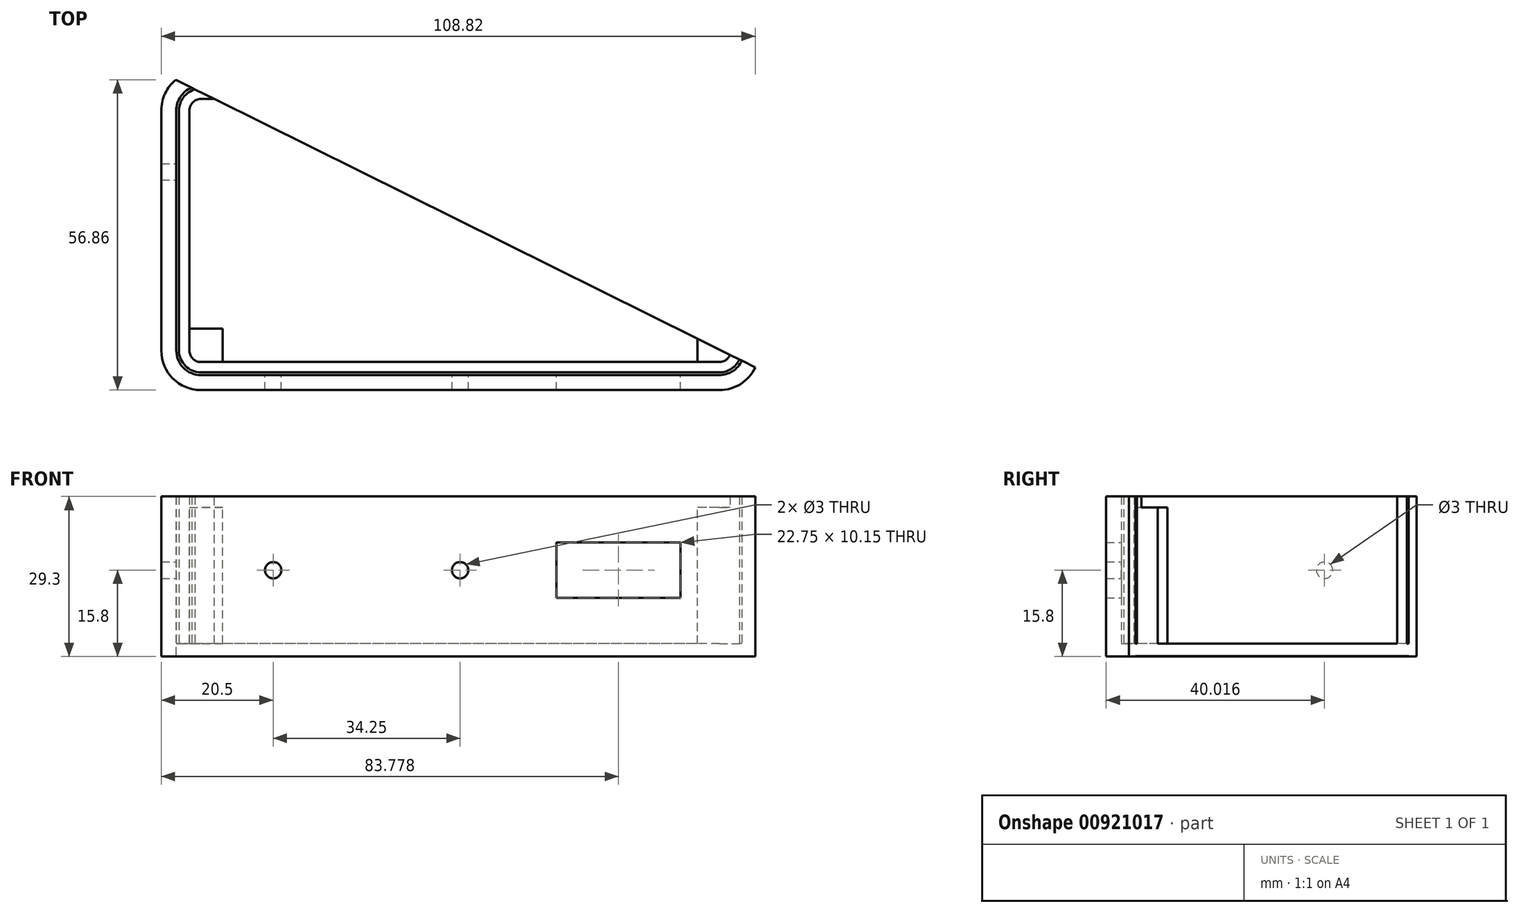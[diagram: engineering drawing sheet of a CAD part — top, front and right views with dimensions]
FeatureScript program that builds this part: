
annotation { "Feature Type Name" : "Feature", "Feature Type Description" : "" }
export const myFeature = defineFeature(function(context is Context, id is Id, definition is map)
    precondition{}
    {
        {
            var Q0;
            Q0=qCreatedBy(makeId("Top.planeOp"),FACE);
            var sketch = newSketch(context, id + "F0", { "sketchPlane" : qUnion([Q0])});
            skLineSegment(sketch, "E0.bottom", {"start": v(47.5, 26) * mm, "end": v(-47.5, 26) * mm});
            skLineSegment(sketch, "E0.top", {"start": v(47.5, -26) * mm, "end": v(-47.5, -26) * mm});
            skLineSegment(sketch, "E0.left", {"start": v(51.5, 22) * mm, "end": v(51.5, -22) * mm});
            skLineSegment(sketch, "E0.right", {"start": v(-51.5, 22) * mm, "end": v(-51.5, -22) * mm});
            skPoint(sketch, "E0.middle", {"position": v(0, 0) * mm});
            skPoint(sketch, "E1.visualSharp", {"position": v(-51.5, 26) * mm});
            skArc(sketch, "E1.filletArc", {"start": v(-47.5, 26) * mm, "mid": v(-50.33, 24.83) * mm, "end": v(-51.5, 22) * mm});
            skPoint(sketch, "E2.visualSharp", {"position": v(-51.5, -26) * mm});
            skArc(sketch, "E2.filletArc", {"start": v(-51.5, -22) * mm, "mid": v(-50.33, -24.83) * mm, "end": v(-47.5, -26) * mm});
            skPoint(sketch, "E3.visualSharp", {"position": v(51.5, -26) * mm});
            skArc(sketch, "E3.filletArc", {"start": v(47.5, -26) * mm, "mid": v(50.33, -24.83) * mm, "end": v(51.5, -22) * mm});
            skPoint(sketch, "E4.visualSharp", {"position": v(51.5, 26) * mm});
            skArc(sketch, "E4.filletArc", {"start": v(51.5, 22) * mm, "mid": v(50.33, 24.83) * mm, "end": v(47.5, 26) * mm});
            skLineSegment(sketch, "E5", {"start": v(-51.5, 18) * mm, "end": v(-43.5, 18) * mm});
            skLineSegment(sketch, "E6", {"start": v(-43.5, 18) * mm, "end": v(-43.5, 26) * mm});
            skLineSegment(sketch, "E7.MirrorCS", {"start": v(-43.5, -18) * mm, "end": v(-43.5, -26) * mm});
            skLineSegment(sketch, "E8.MirrorCS", {"start": v(-51.5, -18) * mm, "end": v(-43.5, -18) * mm});
            skLineSegment(sketch, "E9.MirrorCS", {"start": v(43.5, 18) * mm, "end": v(43.5, 26) * mm});
            skLineSegment(sketch, "E10.MirrorCS", {"start": v(51.5, 18) * mm, "end": v(43.5, 18) * mm});
            skLineSegment(sketch, "E11.MirrorCS", {"start": v(51.5, -18) * mm, "end": v(43.5, -18) * mm});
            skLineSegment(sketch, "E12.MirrorCS", {"start": v(43.5, -18) * mm, "end": v(43.5, -26) * mm});
            skSolve(sketch);
        }
        {
            var Q0;
            {var subQ3=sQuery(id+"F0.wireOp",EDGE,"E5");Q0=makeQuery(id+"F0.imprint","IMPRINT",FACE,{"disambiguationData":[TD([[makeQuery(id+"F0.imprint","IMPRINT",EDGE,{"derivedFrom":subQ3}),-1.0]])]});}
            var Q1;
            {var subQ1=sQuery(id+"F0.wireOp",EDGE,"E1.filletArc");Q1=makeQuery(id+"F0.imprint","IMPRINT",FACE,{"disambiguationData":[TD([[makeQuery(id+"F0.imprint","IMPRINT",EDGE,{"derivedFrom":subQ1}),1.0]])]});}
            var Q2;
            {var subQ0=sQuery(id+"F0.wireOp",EDGE,"E4.filletArc");Q2=makeQuery(id+"F0.imprint","IMPRINT",FACE,{"disambiguationData":[TD([[makeQuery(id+"F0.imprint","IMPRINT",EDGE,{"derivedFrom":subQ0}),1.0]])]});}
            var Q3;
            {var subQ1=sQuery(id+"F0.wireOp",EDGE,"E3.filletArc");Q3=makeQuery(id+"F0.imprint","IMPRINT",FACE,{"disambiguationData":[TD([[makeQuery(id+"F0.imprint","IMPRINT",EDGE,{"derivedFrom":subQ1}),1.0]])]});}
            var Q4;
            {var subQ1=sQuery(id+"F0.wireOp",EDGE,"E2.filletArc");Q4=makeQuery(id+"F0.imprint","IMPRINT",FACE,{"disambiguationData":[TD([[makeQuery(id+"F0.imprint","IMPRINT",EDGE,{"derivedFrom":subQ1}),1.0]])]});}
            extrude(context, id + "F1", {"entities" : qUnion([Q0, Q1, Q2, Q3, Q4]), "depth" : 27 * mm, "offsetDistance" : 25 * mm});
        }
        {
            var Q0;
            Q0=makeQuery(id+"F1.opExtrude","CAP_FACE",FACE,{"disambiguationData":[OSD([sQuery(id+"F0.wireOp",EDGE,"E0.bottom"),sQuery(id+"F0.wireOp",EDGE,"E0.top"),sQuery(id+"F0.wireOp",EDGE,"E0.left"),sQuery(id+"F0.wireOp",EDGE,"E0.right"),sQuery(id+"F0.wireOp",EDGE,"E1.filletArc"),sQuery(id+"F0.wireOp",EDGE,"E2.filletArc"),sQuery(id+"F0.wireOp",EDGE,"E3.filletArc"),sQuery(id+"F0.wireOp",EDGE,"E4.filletArc")])],"isStart":false});
            shell(context, id + "F2", {"entities" : qUnion([Q0]), "thickness" : 1.9 * mm});
        }
        {
            var Q0;
            Q0=makeQuery(id+"F0.imprint","IMPRINT",FACE,{"disambiguationData":[TD([[makeQuery(id+"F0.imprint","IMPRINT",EDGE,{"derivedFrom":sQuery(id+"F0.wireOp",EDGE,"E0.bottom")}),1.0]])]});
            var sketch = newSketch(context, id + "F3", { "sketchPlane" : qUnion([Q0])});
            skLineSegment(sketch, "E13", {"start": v(-51.48, 17.9) * mm, "end": v(-43.48, 17.9) * mm});
            skLineSegment(sketch, "E14", {"start": v(-43.48, 17.9) * mm, "end": v(-43.48, 25.9) * mm});
            skLineSegment(sketch, "E15.MirrorCS", {"start": v(-43.48, -17.9) * mm, "end": v(-43.48, -25.9) * mm});
            skLineSegment(sketch, "E16.MirrorCS", {"start": v(-51.48, -17.9) * mm, "end": v(-43.48, -17.9) * mm});
            skLineSegment(sketch, "E17.MirrorCS", {"start": v(43.48, 17.9) * mm, "end": v(43.48, 25.9) * mm});
            skLineSegment(sketch, "E18.MirrorCS", {"start": v(51.48, 17.9) * mm, "end": v(43.48, 17.9) * mm});
            skLineSegment(sketch, "E19.MirrorCS", {"start": v(51.48, -17.9) * mm, "end": v(43.48, -17.9) * mm});
            skLineSegment(sketch, "E20.MirrorCS", {"start": v(43.48, -17.9) * mm, "end": v(43.48, -25.9) * mm});
            skSolve(sketch);
        }
        {
            var Q0;
            {var subQ0=sQuery(id+"F0.wireOp",EDGE,"E1.filletArc");Q0=makeQuery(id+"F3.imprint","IMPRINT",FACE,{"disambiguationData":[TD([[makeQuery(id+"F3.imprint","IMPRINT",EDGE,{"derivedFrom":makeQuery(id+"F0.imprint","IMPRINT",EDGE,{"derivedFrom":subQ0})}),1.0]])]});}
            var Q1;
            {var subQ1=sQuery(id+"F0.wireOp",EDGE,"E2.filletArc");Q1=makeQuery(id+"F0.imprint","IMPRINT",FACE,{"disambiguationData":[TD([[makeQuery(id+"F0.imprint","IMPRINT",EDGE,{"derivedFrom":subQ1}),1.0]])]});}
            var Q2;
            {var subQ1=sQuery(id+"F0.wireOp",EDGE,"E3.filletArc");Q2=makeQuery(id+"F0.imprint","IMPRINT",FACE,{"disambiguationData":[TD([[makeQuery(id+"F0.imprint","IMPRINT",EDGE,{"derivedFrom":subQ1}),1.0]])]});}
            var Q3;
            {var subQ0=sQuery(id+"F0.wireOp",EDGE,"E4.filletArc");Q3=makeQuery(id+"F0.imprint","IMPRINT",FACE,{"disambiguationData":[TD([[makeQuery(id+"F0.imprint","IMPRINT",EDGE,{"derivedFrom":subQ0}),1.0]])]});}
            extrude(context, id + "F4", {"entities" : qUnion([Q0, Q1, Q2, Q3]), "depth" : 25 * mm, "offsetDistance" : 25 * mm});
        }
        {
            var Q0;
            Q0=makeQuery(id+"F1.opExtrude","SWEPT_FACE",FACE,{"disambiguationData":[OSD([sQuery(id+"F0.wireOp",EDGE,"E0.right")])]});
            var sketch = newSketch(context, id + "F5", { "sketchPlane" : qUnion([Q0])});
            skCircle(sketch, "E21.cCircle", {"center": v(-10.77, 13.5) * mm, "radius": 7.45 * mm, "construction": true});
            skLineSegment(sketch, "E21.0", {"start": v(-4.3, 9.82) * mm, "end": v(-10.72, 6.05) * mm});
            skLineSegment(sketch, "E21.1", {"start": v(-10.72, 6.05) * mm, "end": v(-17.2, 9.73) * mm});
            skLineSegment(sketch, "E21.2", {"start": v(-17.2, 9.73) * mm, "end": v(-17.24, 17.18) * mm});
            skLineSegment(sketch, "E21.3", {"start": v(-17.24, 17.18) * mm, "end": v(-10.81, 20.95) * mm});
            skLineSegment(sketch, "E21.4", {"start": v(-10.81, 20.95) * mm, "end": v(-4.34, 17.27) * mm});
            skLineSegment(sketch, "E21.5", {"start": v(-4.34, 17.27) * mm, "end": v(-4.3, 9.82) * mm});
            skLineSegment(sketch, "E22", {"start": v(22, 13.5) * mm, "end": v(-31.85, 13.5) * mm, "construction": true});
            skCircle(sketch, "E23", {"center": v(-10.77, 13.5) * mm, "radius": 1.5 * mm});
            skSolve(sketch);
        }
        {
            var Q0;
            Q0=makeQuery(id+"F1.opExtrude","SWEPT_FACE",FACE,{"disambiguationData":[OSD([sQuery(id+"F0.wireOp",EDGE,"E0.top")])]});
            var sketch = newSketch(context, id + "F6", { "sketchPlane" : qUnion([Q0])});
            skLineSegment(sketch, "E24", {"start": v(-47.5, 13.5) * mm, "end": v(56.63, 13.5) * mm, "construction": true});
            skCircle(sketch, "E25.cCircle", {"center": v(-34.25, 13.5) * mm, "radius": 8 * mm, "construction": true});
            skLineSegment(sketch, "E25.0", {"start": v(-30.25, 20.43) * mm, "end": v(-26.25, 13.5) * mm});
            skLineSegment(sketch, "E25.1", {"start": v(-26.25, 13.5) * mm, "end": v(-30.25, 6.57) * mm});
            skLineSegment(sketch, "E25.2", {"start": v(-30.25, 6.57) * mm, "end": v(-38.25, 6.57) * mm});
            skLineSegment(sketch, "E25.3", {"start": v(-38.25, 6.57) * mm, "end": v(-42.25, 13.5) * mm});
            skLineSegment(sketch, "E25.4", {"start": v(-42.25, 13.5) * mm, "end": v(-38.25, 20.43) * mm});
            skLineSegment(sketch, "E25.5", {"start": v(-38.25, 20.43) * mm, "end": v(-30.25, 20.43) * mm});
            skCircle(sketch, "E26", {"center": v(0, 13.5) * mm, "radius": 6.38 * mm});
            skLineSegment(sketch, "E27.bottom", {"start": v(40.4, 8.43) * mm, "end": v(17.65, 8.43) * mm});
            skLineSegment(sketch, "E27.top", {"start": v(40.4, 18.58) * mm, "end": v(17.65, 18.58) * mm});
            skLineSegment(sketch, "E27.left", {"start": v(40.4, 8.43) * mm, "end": v(40.4, 18.58) * mm});
            skLineSegment(sketch, "E27.right", {"start": v(17.65, 8.43) * mm, "end": v(17.65, 18.58) * mm});
            skPoint(sketch, "E27.middle", {"position": v(29.03, 13.5) * mm});
            skCircle(sketch, "E28", {"center": v(-34.25, 13.5) * mm, "radius": 1.5 * mm});
            skCircle(sketch, "E29", {"center": v(0, 13.5) * mm, "radius": 1.5 * mm});
            skSolve(sketch);
        }
        {
            var Q0;
            Q0=qCreatedBy(makeId("Top.planeOp"),FACE);
            var sketch = newSketch(context, id + "F7", { "sketchPlane" : qUnion([Q0])});
            skArc(sketch, "E30.0", {"start": v(51.75, 22) * mm, "mid": v(50.5, 25) * mm, "end": v(47.5, 26.25) * mm});
            skLineSegment(sketch, "E30.1", {"start": v(51.75, 22) * mm, "end": v(51.75, -22) * mm});
            skLineSegment(sketch, "E30.2", {"start": v(47.5, 26.25) * mm, "end": v(-47.5, 26.25) * mm});
            skArc(sketch, "E30.3", {"start": v(47.5, -26.25) * mm, "mid": v(50.5, -25) * mm, "end": v(51.75, -22) * mm});
            skArc(sketch, "E30.4", {"start": v(-47.5, 26.25) * mm, "mid": v(-50.5, 25) * mm, "end": v(-51.75, 22) * mm});
            skLineSegment(sketch, "E30.5", {"start": v(-51.75, 22) * mm, "end": v(-51.75, -22) * mm});
            skArc(sketch, "E30.6", {"start": v(-51.75, -22) * mm, "mid": v(-50.5, -25) * mm, "end": v(-47.5, -26.25) * mm});
            skLineSegment(sketch, "E30.7", {"start": v(47.5, -26.25) * mm, "end": v(-47.5, -26.25) * mm});
            skSolve(sketch);
        }
        {
            var Q0;
            Q0=qCreatedBy(makeId("Top.planeOp"),FACE);
            var sketch = newSketch(context, id + "F8", { "sketchPlane" : qUnion([Q0])});
            skArc(sketch, "E31.0", {"start": v(-47.5, 29.25) * mm, "mid": v(-52.63, 27.13) * mm, "end": v(-54.75, 22) * mm});
            skLineSegment(sketch, "E31.1", {"start": v(47.5, 29.25) * mm, "end": v(-47.5, 29.25) * mm});
            skLineSegment(sketch, "E31.2", {"start": v(-54.75, 22) * mm, "end": v(-54.75, -22) * mm});
            skArc(sketch, "E31.3", {"start": v(54.75, 22) * mm, "mid": v(52.63, 27.13) * mm, "end": v(47.5, 29.25) * mm});
            skArc(sketch, "E31.4", {"start": v(-54.75, -22) * mm, "mid": v(-52.63, -27.13) * mm, "end": v(-47.5, -29.25) * mm});
            skLineSegment(sketch, "E31.5", {"start": v(47.5, -29.25) * mm, "end": v(-47.5, -29.25) * mm});
            skArc(sketch, "E31.6", {"start": v(47.5, -29.25) * mm, "mid": v(52.63, -27.13) * mm, "end": v(54.75, -22) * mm});
            skLineSegment(sketch, "E31.7", {"start": v(54.75, 22) * mm, "end": v(54.75, -22) * mm});
            skSolve(sketch);
        }
        {
            var Q0;
            Q0=makeQuery(id+"F8.imprint","IMPRINT",FACE,{"disambiguationData":[TD([[makeQuery(id+"F8.imprint","IMPRINT",EDGE,{"derivedFrom":sQuery(id+"F8.wireOp",EDGE,"E31.0")}),1.0]])]});
            extrude(context, id + "F9", {"entities" : qUnion([Q0]), "depth" : 27 * mm, "offsetDistance" : 25 * mm});
        }
        {
            var Q0;
            Q0=makeQuery(id+"F9.opExtrude","CAP_FACE",FACE,{"disambiguationData":[OSD([sQuery(id+"F8.wireOp",EDGE,"E31.0"),sQuery(id+"F8.wireOp",EDGE,"E31.1"),sQuery(id+"F8.wireOp",EDGE,"E31.2"),sQuery(id+"F8.wireOp",EDGE,"E31.3"),sQuery(id+"F8.wireOp",EDGE,"E31.4"),sQuery(id+"F8.wireOp",EDGE,"E31.5"),sQuery(id+"F8.wireOp",EDGE,"E31.6"),sQuery(id+"F8.wireOp",EDGE,"E31.7")])],"isStart":false});
            shell(context, id + "F10", {"entities" : qUnion([Q0]), "thickness" : 2.75 * mm});
        }
        {
            var Q0;
            Q0=makeQuery(id+"F6.imprint","IMPRINT",FACE,{"disambiguationData":[TD([[makeQuery(id+"F6.imprint","IMPRINT",EDGE,{"derivedFrom":sQuery(id+"F6.wireOp",EDGE,"E28")}),1.0]])]});
            var Q1;
            Q1=makeQuery(id+"F6.imprint","IMPRINT",FACE,{"disambiguationData":[TD([[makeQuery(id+"F6.imprint","IMPRINT",EDGE,{"derivedFrom":sQuery(id+"F6.wireOp",EDGE,"E29")}),1.0]])]});
            var Q2;
            Q2=makeQuery(id+"F6.imprint","IMPRINT",FACE,{"disambiguationData":[TD([[makeQuery(id+"F6.imprint","IMPRINT",EDGE,{"derivedFrom":sQuery(id+"F6.wireOp",EDGE,"E27.bottom")}),-1.0]])]});
            extrude(context, id + "F11", {"entities" : qUnion([Q0, Q1, Q2]), "operationType" : NewBodyOperationType.REMOVE, "depth" : 25 * mm, "offsetDistance" : 25 * mm});
        }
        {
            var Q0;
            Q0=makeQuery(id+"F5.imprint","IMPRINT",FACE,{"disambiguationData":[TD([[makeQuery(id+"F5.imprint","IMPRINT",EDGE,{"derivedFrom":sQuery(id+"F5.wireOp",EDGE,"E23")}),1.0]])]});
            extrude(context, id + "F12", {"entities" : qUnion([Q0]), "operationType" : NewBodyOperationType.REMOVE, "depth" : 25 * mm, "offsetDistance" : 25 * mm});
        }
        {
            var Q0;
            Q0=qCreatedBy(makeId("Top.planeOp"),FACE);
            var sketch = newSketch(context, id + "F13", { "sketchPlane" : qUnion([Q0])});
            skLineSegment(sketch, "E32", {"start": v(-55.6, 29.35) * mm, "end": v(62.09, -29.05) * mm});
            skLineSegment(sketch, "E33", {"start": v(-55.6, 29.35) * mm, "end": v(65.33, 29.35) * mm});
            skLineSegment(sketch, "E34", {"start": v(65.33, 29.35) * mm, "end": v(62.09, -29.05) * mm});
            skSolve(sketch);
        }
        {
            var Q0;
            Q0 = qSketchRegion(id + "F13", true);
            extrude(context, id + "F14", {"entities" : qUnion([Q0]), "operationType" : NewBodyOperationType.REMOVE, "depth" : 30 * mm, "offsetDistance" : 25 * mm});
        }
        {
            var Q0;
            Q0=makeQuery(id+"F10.opShell","OFFSET_FACE",FACE,{"disambiguationData":[OSD([sQuery(id+"F8.wireOp",EDGE,"E31.0"),sQuery(id+"F8.wireOp",EDGE,"E31.1"),sQuery(id+"F8.wireOp",EDGE,"E31.2"),sQuery(id+"F8.wireOp",EDGE,"E31.3"),sQuery(id+"F8.wireOp",EDGE,"E31.4"),sQuery(id+"F8.wireOp",EDGE,"E31.5"),sQuery(id+"F8.wireOp",EDGE,"E31.6"),sQuery(id+"F8.wireOp",EDGE,"E31.7")])]});
            extrude(context, id + "F15", {"entities" : qUnion([Q0]), "operationType" : NewBodyOperationType.ADD, "oppositeDirection" : true, "depth" : 5 * mm, "offsetDistance" : 25 * mm});
        }
        {
            var Q0;
            Q0=makeQuery(id+"F9.opExtrude","CAP_FACE",FACE,{"disambiguationData":[OSD([sQuery(id+"F8.wireOp",EDGE,"E31.0"),sQuery(id+"F8.wireOp",EDGE,"E31.1"),sQuery(id+"F8.wireOp",EDGE,"E31.2"),sQuery(id+"F8.wireOp",EDGE,"E31.3"),sQuery(id+"F8.wireOp",EDGE,"E31.4"),sQuery(id+"F8.wireOp",EDGE,"E31.5"),sQuery(id+"F8.wireOp",EDGE,"E31.6"),sQuery(id+"F8.wireOp",EDGE,"E31.7")])],"isStart":true});
            extrude(context, id + "F16", {"entities" : qUnion([Q0]), "operationType" : NewBodyOperationType.ADD, "depth" : 2.3 * mm, "offsetDistance" : 25 * mm});
        }
        {
            var Q0;
            Q0=makeQuery(id+"F10.opShell","OFFSET_FACE",FACE,{"disambiguationData":[OSD([sQuery(id+"F8.wireOp",EDGE,"E31.0"),sQuery(id+"F8.wireOp",EDGE,"E31.1"),sQuery(id+"F8.wireOp",EDGE,"E31.2"),sQuery(id+"F8.wireOp",EDGE,"E31.3"),sQuery(id+"F8.wireOp",EDGE,"E31.4"),sQuery(id+"F8.wireOp",EDGE,"E31.5"),sQuery(id+"F8.wireOp",EDGE,"E31.6"),sQuery(id+"F8.wireOp",EDGE,"E31.7")])]});
            extrude(context, id + "F17", {"entities" : qUnion([Q0]), "operationType" : NewBodyOperationType.REMOVE, "oppositeDirection" : true, "depth" : 2.7 * mm, "offsetDistance" : 25 * mm});
        }
    });
